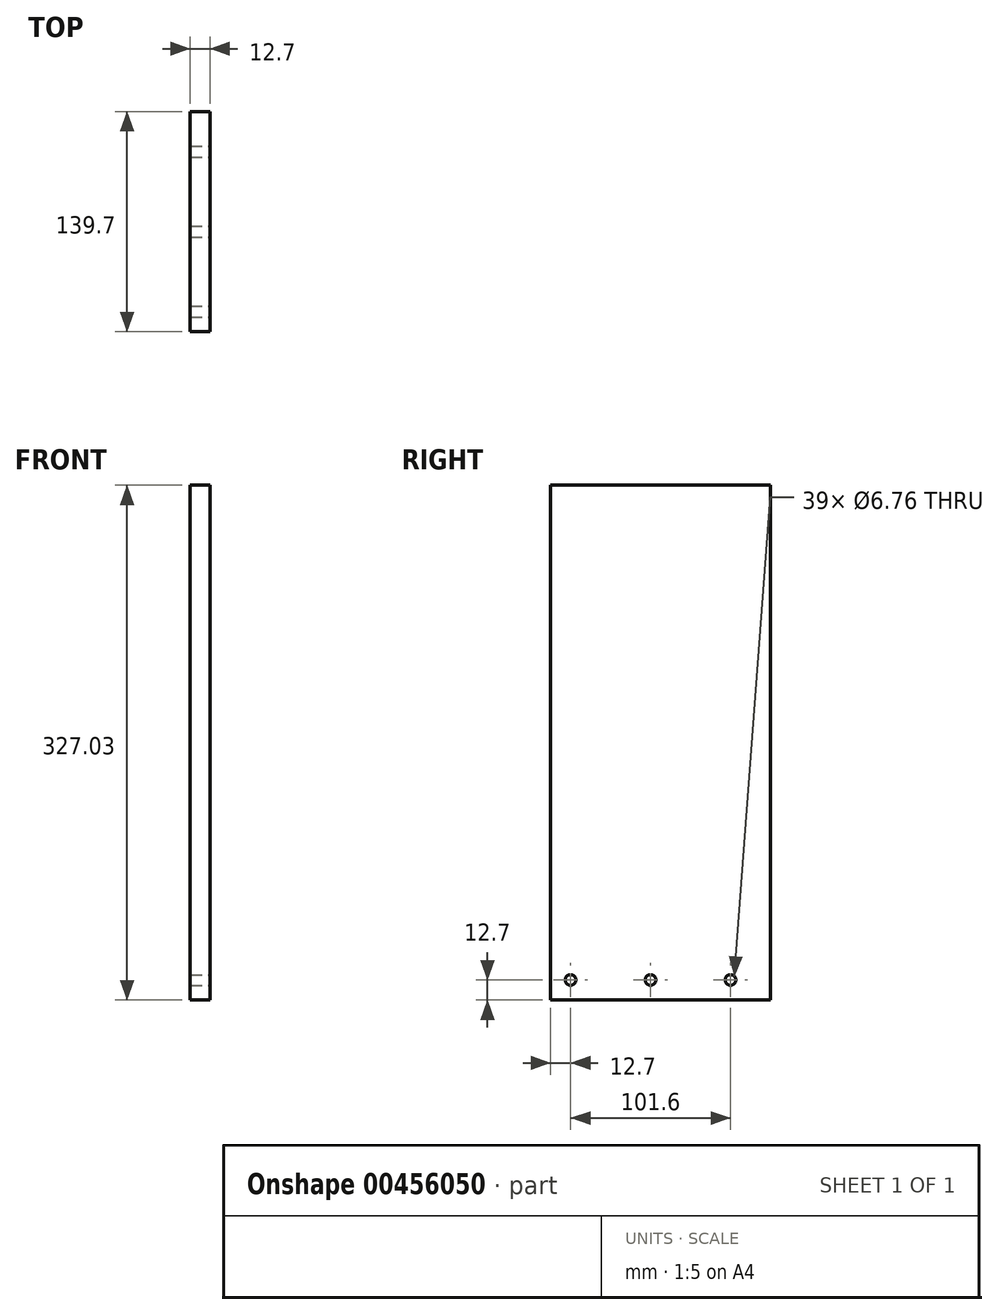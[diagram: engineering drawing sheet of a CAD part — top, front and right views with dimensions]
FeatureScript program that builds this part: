
annotation { "Feature Type Name" : "Feature", "Feature Type Description" : "" }
export const myFeature = defineFeature(function(context is Context, id is Id, definition is map)
    precondition{}
    {
        {
            var Q0;
            Q0=qCreatedBy(makeId("Right.planeOp"),FACE);
            var sketch = newSketch(context, id + "F0", { "sketchPlane" : qUnion([Q0])});
            skLineSegment(sketch, "E0.bottom", {"start": v(0, 0) * mm, "end": v(-152.4, 0) * mm});
            skLineSegment(sketch, "E0.top", {"start": v(0, 339.73) * mm, "end": v(-152.4, 339.73) * mm});
            skLineSegment(sketch, "E0.left", {"start": v(0, 0) * mm, "end": v(0, 339.73) * mm});
            skLineSegment(sketch, "E0.right", {"start": v(-152.4, 0) * mm, "end": v(-152.4, 339.73) * mm});
            skLineSegment(sketch, "E1", {"start": v(-152.4, 12.7) * mm, "end": v(0, 12.7) * mm});
            skLineSegment(sketch, "E2", {"start": v(-152.4, 339.73) * mm, "end": v(-12.7, 473.08) * mm});
            skLineSegment(sketch, "E3", {"start": v(-12.7, 473.08) * mm, "end": v(0, 473.08) * mm});
            skLineSegment(sketch, "E4", {"start": v(0, 473.08) * mm, "end": v(0, 339.73) * mm});
            skLineSegment(sketch, "E5", {"start": v(-139.7, 351.85) * mm, "end": v(-139.7, 0) * mm});
            skLineSegment(sketch, "E6", {"start": v(-12.7, 473.08) * mm, "end": v(-12.7, 0) * mm});
            skSolve(sketch);
        }
        {
            var Q0;
            {var subQ0=sQuery(id+"F0.wireOp",EDGE,"E6");var subQ1=sQuery(id+"F0.wireOp",EDGE,"E0.top");var subQ2=makeQuery(id+"F0.imprint","INTERSECT",VERTEX,{"derivedFrom":[subQ1,subQ0]});Q0=makeQuery(id+"F0.imprint","IMPRINT",FACE,{"disambiguationData":[TD([[makeQuery(id+"F0.imprint","IMPRINT",EDGE,{"disambiguationData":[TD([[subQ2,-1.0]])],"derivedFrom":subQ1}),1.0]])]});}
            var Q1;
            {var subQ0=sQuery(id+"F0.wireOp",EDGE,"E0.left");var subQ5=sQuery(id+"F0.wireOp",EDGE,"E1");var subQ6=makeQuery(id+"F0.imprint","INTERSECT",VERTEX,{"derivedFrom":[subQ0,subQ5]});Q1=makeQuery(id+"F0.imprint","IMPRINT",FACE,{"disambiguationData":[TD([[makeQuery(id+"F0.imprint","IMPRINT",EDGE,{"disambiguationData":[TD([[subQ6,1.0]])],"derivedFrom":subQ5}),1.0]])]});}
            extrude(context, id + "F1", {"entities" : qUnion([Q0, Q1]), "depth" : 12.7 * mm});
        }
        {
            var Q0;
            Q0=makeQuery(id+"F1.opExtrude","CAP_FACE",FACE,{"disambiguationData":[OSD([sQuery(id+"F0.wireOp",EDGE,"E0.top"),sQuery(id+"F0.wireOp",EDGE,"E0.left"),sQuery(id+"F0.wireOp",EDGE,"E1"),sQuery(id+"F0.wireOp",EDGE,"E5")])],"isStart":false});
            var sketch = newSketch(context, id + "F2", { "sketchPlane" : qUnion([Q0])});
            skLineSegment(sketch, "E7", {"start": v(-139.7, 25.4) * mm, "end": v(0, 25.4) * mm, "construction": true});
            skPoint(sketch, "E8", {"position": v(-127, 25.4) * mm});
            skPoint(sketch, "E9.1.0.0", {"position": v(-76.2, 25.4) * mm});
            skPoint(sketch, "E9.2.0.0", {"position": v(-25.4, 25.4) * mm});
            skLineSegment(sketch, "E9.direction1", {"start": v(-127, 25.4) * mm, "end": v(-76.2, 25.4) * mm, "construction": true});
            skSolve(sketch);
        }
        {
            var Q0;
            Q0=sQuery(id+"F2.wireOp",VERTEX,"E8");
            var Q1;
            Q1=sQuery(id+"F2.wireOp",VERTEX,"E9.1.0.0");
            var Q2;
            Q2=sQuery(id+"F2.wireOp",VERTEX,"E9.2.0.0");
            var Q3;
            Q3=makeQuery(id+"F1.opExtrude","SWEPT_BODY",BODY,{"disambiguationData":[OSD([sQuery(id+"F0.wireOp",EDGE,"E0.top"),sQuery(id+"F0.wireOp",EDGE,"E0.left"),sQuery(id+"F0.wireOp",EDGE,"E1"),sQuery(id+"F0.wireOp",EDGE,"E5")])]});
            hole(context, id + "F3", {"style" : HoleStyle.SIMPLE, "endStyle" : HoleEndStyle.THROUGH, "standardTappedOrClearance" : lookupTablePath({ "standard" : "ANSI", "fit" : "Normal (ASME)", "size" : "1/4", "type" : "Clearance" }), "standardBlindInLast" : lookupTablePath({ "fit" : "Free", "standard" : "ANSI", "size" : "1/4", "type" : "Clearance" }), "holeDiameter" : 6.76 * mm, "isTappedThrough" : true, "tappedDepth" : 8.9 * mm, "tapClearance" : 3, "locations" : qUnion([Q0, Q1, Q2]), "scope" : qUnion([Q3])});
        }
    });
